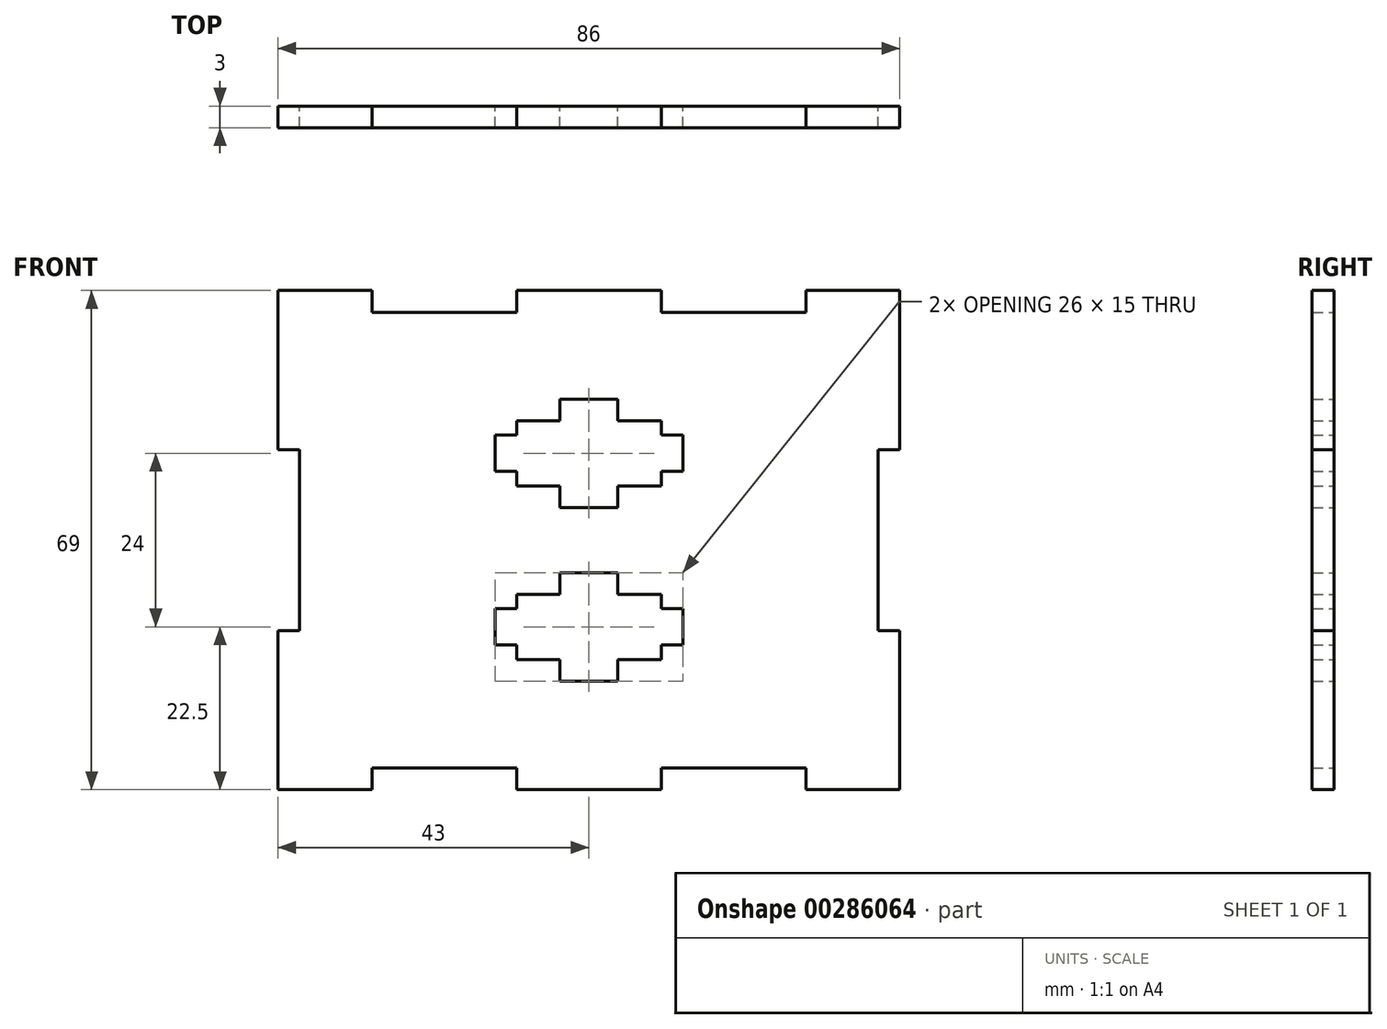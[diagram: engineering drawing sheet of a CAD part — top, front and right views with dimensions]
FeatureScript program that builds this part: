
annotation { "Feature Type Name" : "Feature", "Feature Type Description" : "" }
export const myFeature = defineFeature(function(context is Context, id is Id, definition is map)
    precondition{}
    {
        {
            var Q0;
            Q0=qCreatedBy(makeId("Front.planeOp"),FACE);
            var sketch = newSketch(context, id + "F0", { "sketchPlane" : qUnion([Q0])});
            skLineSegment(sketch, "E0", {"start": v(0, 34.5) * mm, "end": v(-10, 34.5) * mm});
            skLineSegment(sketch, "E1", {"start": v(-10, 34.5) * mm, "end": v(-10, 31.5) * mm});
            skLineSegment(sketch, "E2", {"start": v(-10, 31.5) * mm, "end": v(-30, 31.5) * mm});
            skLineSegment(sketch, "E3", {"start": v(-30, 31.5) * mm, "end": v(-30, 34.5) * mm});
            skLineSegment(sketch, "E4", {"start": v(-30, 34.5) * mm, "end": v(-43, 34.5) * mm});
            skLineSegment(sketch, "E5", {"start": v(-43, 34.5) * mm, "end": v(-43, 12.5) * mm});
            skLineSegment(sketch, "E6", {"start": v(-43, 12.5) * mm, "end": v(-40, 12.5) * mm});
            skLineSegment(sketch, "E7", {"start": v(-40, 12.5) * mm, "end": v(-40, 0) * mm});
            skLineSegment(sketch, "E8", {"start": v(-40, 0) * mm, "end": v(0, 0) * mm, "construction": true});
            skLineSegment(sketch, "E9.MirrorCS", {"start": v(0, 34.5) * mm, "end": v(10, 34.5) * mm});
            skLineSegment(sketch, "E10.MirrorCS", {"start": v(40, 12.5) * mm, "end": v(40, 0) * mm});
            skLineSegment(sketch, "E11.MirrorCS", {"start": v(43, 12.5) * mm, "end": v(40, 12.5) * mm});
            skLineSegment(sketch, "E12.MirrorCS", {"start": v(10, 34.5) * mm, "end": v(10, 31.5) * mm});
            skLineSegment(sketch, "E13.MirrorCS", {"start": v(30, 34.5) * mm, "end": v(43, 34.5) * mm});
            skLineSegment(sketch, "E14.MirrorCS", {"start": v(10, 31.5) * mm, "end": v(30, 31.5) * mm});
            skLineSegment(sketch, "E15.MirrorCS", {"start": v(43, 34.5) * mm, "end": v(43, 12.5) * mm});
            skLineSegment(sketch, "E16.MirrorCS", {"start": v(30, 31.5) * mm, "end": v(30, 34.5) * mm});
            skLineSegment(sketch, "E17.MirrorCS", {"start": v(10, -31.5) * mm, "end": v(30, -31.5) * mm});
            skLineSegment(sketch, "E18.MirrorCS", {"start": v(43, -34.5) * mm, "end": v(43, -12.5) * mm});
            skLineSegment(sketch, "E19.MirrorCS", {"start": v(30, -34.5) * mm, "end": v(43, -34.5) * mm});
            skLineSegment(sketch, "E20.MirrorCS", {"start": v(0, -34.5) * mm, "end": v(-10, -34.5) * mm});
            skLineSegment(sketch, "E21.MirrorCS", {"start": v(-10, -34.5) * mm, "end": v(-10, -31.5) * mm});
            skLineSegment(sketch, "E22.MirrorCS", {"start": v(-43, -12.5) * mm, "end": v(-40, -12.5) * mm});
            skLineSegment(sketch, "E23.MirrorCS", {"start": v(-10, -31.5) * mm, "end": v(-30, -31.5) * mm});
            skLineSegment(sketch, "E24.MirrorCS", {"start": v(-30, -31.5) * mm, "end": v(-30, -34.5) * mm});
            skLineSegment(sketch, "E25.MirrorCS", {"start": v(-40, -12.5) * mm, "end": v(-40, 0) * mm});
            skLineSegment(sketch, "E26.MirrorCS", {"start": v(30, -31.5) * mm, "end": v(30, -34.5) * mm});
            skLineSegment(sketch, "E27.MirrorCS", {"start": v(-43, -34.5) * mm, "end": v(-43, -12.5) * mm});
            skLineSegment(sketch, "E28.MirrorCS", {"start": v(10, -34.5) * mm, "end": v(10, -31.5) * mm});
            skLineSegment(sketch, "E29.MirrorCS", {"start": v(43, -12.5) * mm, "end": v(40, -12.5) * mm});
            skLineSegment(sketch, "E30.MirrorCS", {"start": v(40, -12.5) * mm, "end": v(40, 0) * mm});
            skLineSegment(sketch, "E31.MirrorCS", {"start": v(0, -34.5) * mm, "end": v(10, -34.5) * mm});
            skLineSegment(sketch, "E32.MirrorCS", {"start": v(-30, -34.5) * mm, "end": v(-43, -34.5) * mm});
            skLineSegment(sketch, "E33.bottom", {"start": v(-10, 7.5) * mm, "end": v(-10, 16.5) * mm, "construction": true});
            skLineSegment(sketch, "E33.top", {"start": v(10, 7.5) * mm, "end": v(10, 16.5) * mm, "construction": true});
            skLineSegment(sketch, "E33.left", {"start": v(-10, 7.5) * mm, "end": v(10, 7.5) * mm, "construction": true});
            skLineSegment(sketch, "E33.right", {"start": v(-10, 16.5) * mm, "end": v(10, 16.5) * mm, "construction": true});
            skPoint(sketch, "E33.middle", {"position": v(0, 12) * mm});
            skLineSegment(sketch, "E34", {"start": v(10, 16.5) * mm, "end": v(4, 16.5) * mm});
            skLineSegment(sketch, "E35", {"start": v(4, 16.5) * mm, "end": v(4, 19.5) * mm});
            skLineSegment(sketch, "E36", {"start": v(4, 19.5) * mm, "end": v(0, 19.5) * mm});
            skLineSegment(sketch, "E37", {"start": v(10, 16.5) * mm, "end": v(10, 14.5) * mm});
            skLineSegment(sketch, "E38", {"start": v(10, 14.5) * mm, "end": v(13, 14.5) * mm});
            skLineSegment(sketch, "E39", {"start": v(13, 14.5) * mm, "end": v(13, 9.5) * mm});
            skLineSegment(sketch, "E40", {"start": v(13, 9.5) * mm, "end": v(10, 9.5) * mm});
            skLineSegment(sketch, "E41", {"start": v(10, 9.5) * mm, "end": v(10, 7.5) * mm});
            skLineSegment(sketch, "E42", {"start": v(10, 7.5) * mm, "end": v(4, 7.5) * mm});
            skLineSegment(sketch, "E43", {"start": v(4, 7.5) * mm, "end": v(4, 4.5) * mm});
            skLineSegment(sketch, "E44", {"start": v(4, 4.5) * mm, "end": v(0, 4.5) * mm});
            skLineSegment(sketch, "E45", {"start": v(0, 0) * mm, "end": v(0, 34.5) * mm, "construction": true});
            skLineSegment(sketch, "E46.MirrorCS", {"start": v(0, 0) * mm, "end": v(0, -34.5) * mm, "construction": true});
            skLineSegment(sketch, "E47.MirrorCS", {"start": v(-10, 16.5) * mm, "end": v(-10, 14.5) * mm});
            skLineSegment(sketch, "E48.MirrorCS", {"start": v(-10, 9.5) * mm, "end": v(-10, 7.5) * mm});
            skLineSegment(sketch, "E49.MirrorCS", {"start": v(-4, 16.5) * mm, "end": v(-4, 19.5) * mm});
            skLineSegment(sketch, "E50.MirrorCS", {"start": v(-13, 14.5) * mm, "end": v(-13, 9.5) * mm});
            skLineSegment(sketch, "E51.MirrorCS", {"start": v(-4, 19.5) * mm, "end": v(0, 19.5) * mm});
            skLineSegment(sketch, "E52.MirrorCS", {"start": v(-10, 16.5) * mm, "end": v(-4, 16.5) * mm});
            skLineSegment(sketch, "E53.MirrorCS", {"start": v(-13, 9.5) * mm, "end": v(-10, 9.5) * mm});
            skLineSegment(sketch, "E54.MirrorCS", {"start": v(-10, 7.5) * mm, "end": v(-4, 7.5) * mm});
            skLineSegment(sketch, "E55.MirrorCS", {"start": v(-10, 14.5) * mm, "end": v(-13, 14.5) * mm});
            skLineSegment(sketch, "E56.MirrorCS", {"start": v(-4, 4.5) * mm, "end": v(0, 4.5) * mm});
            skLineSegment(sketch, "E57.MirrorCS", {"start": v(-4, 7.5) * mm, "end": v(-4, 4.5) * mm});
            skLineSegment(sketch, "E58.MirrorCS", {"start": v(-13, -9.5) * mm, "end": v(-10, -9.5) * mm});
            skLineSegment(sketch, "E59.MirrorCS", {"start": v(-10, -9.5) * mm, "end": v(-10, -7.5) * mm});
            skLineSegment(sketch, "E60.MirrorCS", {"start": v(-10, -16.5) * mm, "end": v(-10, -14.5) * mm});
            skLineSegment(sketch, "E61.MirrorCS", {"start": v(10, -16.5) * mm, "end": v(10, -14.5) * mm});
            skLineSegment(sketch, "E62.MirrorCS", {"start": v(10, -9.5) * mm, "end": v(10, -7.5) * mm});
            skLineSegment(sketch, "E63.MirrorCS", {"start": v(10, -16.5) * mm, "end": v(4, -16.5) * mm});
            skPoint(sketch, "E64.MirrorP", {"position": v(0, -12) * mm});
            skLineSegment(sketch, "E65.MirrorCS", {"start": v(-10, -16.5) * mm, "end": v(-4, -16.5) * mm});
            skLineSegment(sketch, "E66.MirrorCS", {"start": v(-10, -7.5) * mm, "end": v(-4, -7.5) * mm});
            skLineSegment(sketch, "E67.MirrorCS", {"start": v(10, -7.5) * mm, "end": v(4, -7.5) * mm});
            skLineSegment(sketch, "E68.MirrorCS", {"start": v(13, -9.5) * mm, "end": v(10, -9.5) * mm});
            skLineSegment(sketch, "E69.MirrorCS", {"start": v(-10, -7.5) * mm, "end": v(10, -7.5) * mm, "construction": true});
            skLineSegment(sketch, "E70.MirrorCS", {"start": v(4, -7.5) * mm, "end": v(4, -4.5) * mm});
            skLineSegment(sketch, "E71.MirrorCS", {"start": v(4, -19.5) * mm, "end": v(0, -19.5) * mm});
            skLineSegment(sketch, "E72.MirrorCS", {"start": v(-10, -7.5) * mm, "end": v(-10, -16.5) * mm, "construction": true});
            skLineSegment(sketch, "E73.MirrorCS", {"start": v(13, -14.5) * mm, "end": v(13, -9.5) * mm});
            skLineSegment(sketch, "E74.MirrorCS", {"start": v(-4, -4.5) * mm, "end": v(0, -4.5) * mm});
            skLineSegment(sketch, "E75.MirrorCS", {"start": v(-4, -7.5) * mm, "end": v(-4, -4.5) * mm});
            skLineSegment(sketch, "E76.MirrorCS", {"start": v(-10, -14.5) * mm, "end": v(-13, -14.5) * mm});
            skLineSegment(sketch, "E77.MirrorCS", {"start": v(10, -7.5) * mm, "end": v(10, -16.5) * mm, "construction": true});
            skLineSegment(sketch, "E78.MirrorCS", {"start": v(-10, -16.5) * mm, "end": v(10, -16.5) * mm, "construction": true});
            skLineSegment(sketch, "E79.MirrorCS", {"start": v(-13, -14.5) * mm, "end": v(-13, -9.5) * mm});
            skLineSegment(sketch, "E80.MirrorCS", {"start": v(10, -14.5) * mm, "end": v(13, -14.5) * mm});
            skLineSegment(sketch, "E81.MirrorCS", {"start": v(4, -16.5) * mm, "end": v(4, -19.5) * mm});
            skLineSegment(sketch, "E82.MirrorCS", {"start": v(-4, -19.5) * mm, "end": v(0, -19.5) * mm});
            skLineSegment(sketch, "E83.MirrorCS", {"start": v(4, -4.5) * mm, "end": v(0, -4.5) * mm});
            skLineSegment(sketch, "E84.MirrorCS", {"start": v(-4, -16.5) * mm, "end": v(-4, -19.5) * mm});
            skSolve(sketch);
        }
        {
            var Q0;
            Q0 = qSketchRegion(id + "F0", true);
            extrude(context, id + "F1", {"entities" : qUnion([Q0]), "depth" : 3 * mm});
        }
    });
